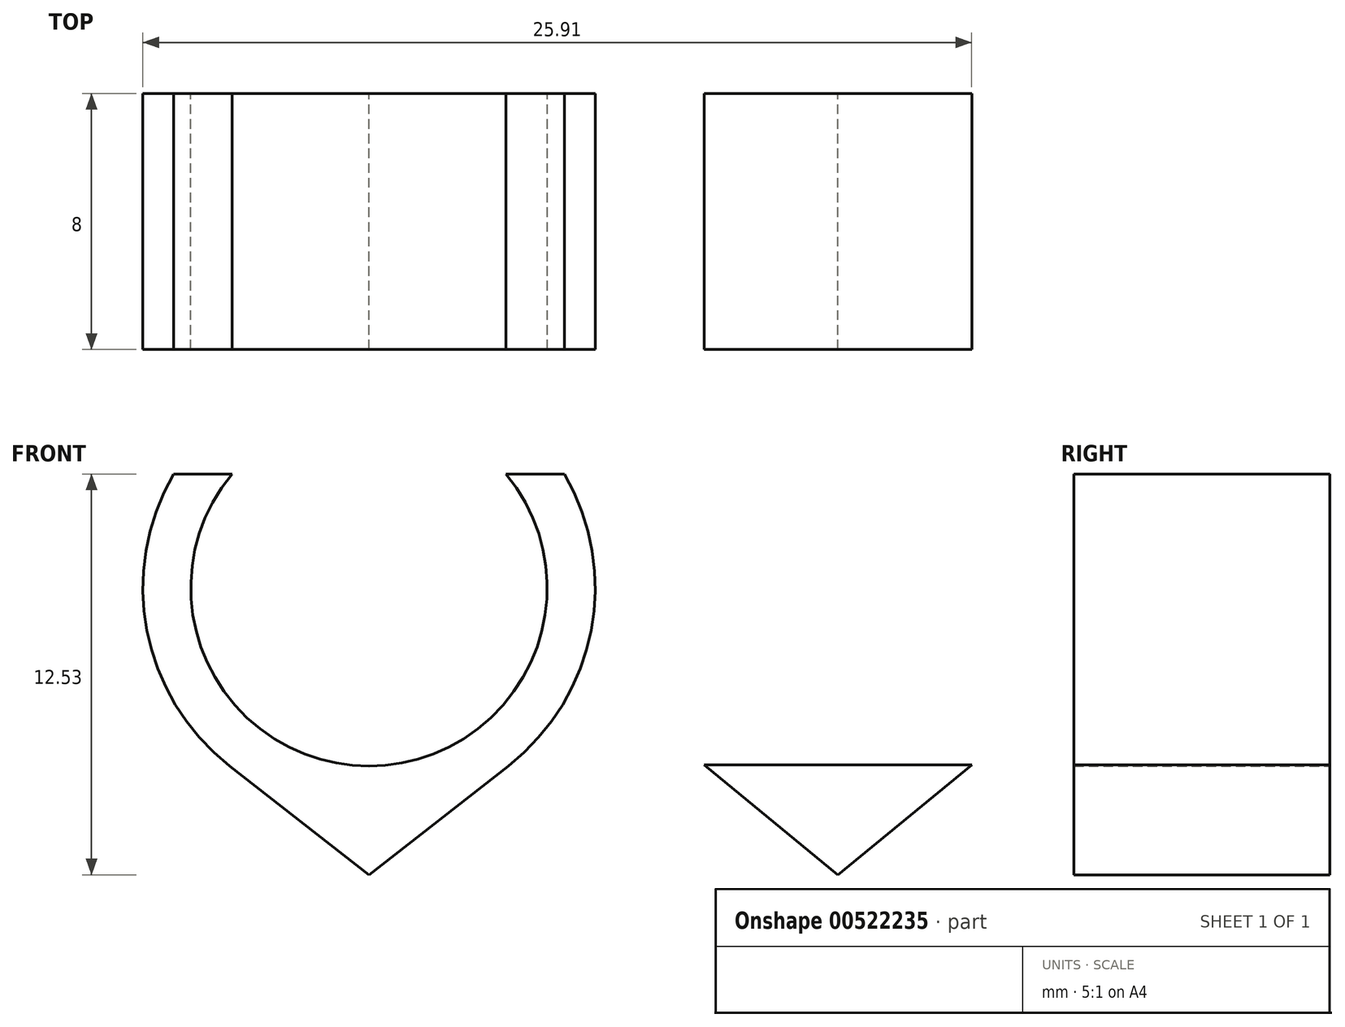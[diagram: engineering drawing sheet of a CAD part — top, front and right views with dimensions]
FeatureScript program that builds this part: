
annotation { "Feature Type Name" : "Feature", "Feature Type Description" : "" }
export const myFeature = defineFeature(function(context is Context, id is Id, definition is map)
    precondition{}
    {
        {
            var Q0;
            Q0=qCreatedBy(makeId("Front.planeOp"),FACE);
            var sketch = newSketch(context, id + "F0", { "sketchPlane" : qUnion([Q0])});
            skArc(sketch, "E0", {"start": v(-6.1, 12.53) * mm, "mid": v(0, 1.9) * mm, "end": v(6.1, 12.53) * mm});
            skLineSegment(sketch, "E1", {"start": v(-4.35, 3.4) * mm, "end": v(0, 0) * mm});
            skLineSegment(sketch, "E2", {"start": v(0, 0) * mm, "end": v(4.35, 3.4) * mm});
            skLineSegment(sketch, "E3", {"start": v(6.1, 12.53) * mm, "end": v(-6.1, 12.53) * mm});
            skArc(sketch, "E4.0", {"start": v(-4.29, 12.53) * mm, "mid": v(0, 3.4) * mm, "end": v(4.29, 12.53) * mm});
            skLineSegment(sketch, "E5", {"start": v(-5, 0) * mm, "end": v(5, 0) * mm});
            skArc(sketch, "E6", {"start": v(8.79, 11.53) * mm, "mid": v(14.66, 1.94) * mm, "end": v(20.53, 11.53) * mm});
            skLineSegment(sketch, "E7", {"start": v(10.47, 3.44) * mm, "end": v(14.66, 0) * mm});
            skLineSegment(sketch, "E8", {"start": v(14.66, 0) * mm, "end": v(18.84, 3.44) * mm});
            skLineSegment(sketch, "E9", {"start": v(20.53, 11.53) * mm, "end": v(8.79, 11.53) * mm});
            skArc(sketch, "E10.0", {"start": v(10.54, 11.53) * mm, "mid": v(14.66, 3.44) * mm, "end": v(18.78, 11.53) * mm});
            skLineSegment(sketch, "E11", {"start": v(9.66, 0) * mm, "end": v(19.66, 0) * mm});
            skLineSegment(sketch, "E12", {"start": v(14.66, 8.53) * mm, "end": v(14.66, 0) * mm});
            skLineSegment(sketch, "E13", {"start": v(-4.35, 3.4) * mm, "end": v(4.35, 3.4) * mm});
            skLineSegment(sketch, "E14", {"start": v(0, 8.97) * mm, "end": v(0, 0) * mm});
            skLineSegment(sketch, "E15", {"start": v(10.47, 3.44) * mm, "end": v(18.84, 3.44) * mm});
            skSolve(sketch);
        }
        {
            var Q0;
            Q0=sQuery(id+"F0.wireOp",EDGE,"E5");
            var Q1;
            {var subQ0=sQuery(id+"F0.wireOp",EDGE,"E1");Q1=makeQuery(id+"F0.imprint","IMPRINT",FACE,{"disambiguationData":[TD([[makeQuery(id+"F0.imprint","IMPRINT",EDGE,{"derivedFrom":subQ0}),1.0]])]});}
            cPlane(context, id + "F1", {"entities" : qUnion([Q0, Q1]), "cplaneType" : CPlaneType.LINE_ANGLE, "offset" : 25 * mm, "angle" : 90 * degree, "width" : 150 * mm, "height" : 150 * mm});
        }
        {
            var Q0;
            Q0=qCreatedBy(id+"F1.planeOp",FACE);
            var sketch = newSketch(context, id + "F2", { "sketchPlane" : qUnion([Q0])});
            skLineSegment(sketch, "E16", {"start": v(0, 0) * mm, "end": v(0, 8) * mm});
            skLineSegment(sketch, "E17.0", {"start": v(9.66, 0) * mm, "end": v(19.66, 0) * mm});
            skLineSegment(sketch, "E18", {"start": v(14.66, 0) * mm, "end": v(14.66, 8) * mm});
            skSolve(sketch);
        }
        {
            var Q0;
            {var subQ0=sQuery(id+"F0.wireOp",EDGE,"E3");var subQ1=sQuery(id+"F0.wireOp",EDGE,"E0");var subQ2=makeQuery(id+"F0.imprint","INTERSECT",VERTEX,{"disambiguationData":[OD(0.0)],"derivedFrom":[subQ1,subQ0]});Q0=makeQuery(id+"F0.imprint","IMPRINT",FACE,{"disambiguationData":[TD([[makeQuery(id+"F0.imprint","IMPRINT",EDGE,{"disambiguationData":[TD([[subQ2,1.0]])],"derivedFrom":subQ0}),1.0]])]});}
            var Q1;
            {var subQ1=sQuery(id+"F0.wireOp",EDGE,"E0");var subQ3=sQuery(id+"F0.wireOp",EDGE,"E14");var subQ4=makeQuery(id+"F0.imprint","INTERSECT",VERTEX,{"derivedFrom":[subQ1,subQ3]});Q1=makeQuery(id+"F0.imprint","IMPRINT",FACE,{"disambiguationData":[TD([[makeQuery(id+"F0.imprint","IMPRINT",EDGE,{"disambiguationData":[TD([[subQ4,1.0]])],"derivedFrom":subQ1}),1.0]])]});}
            var Q2;
            {var subQ0=sQuery(id+"F0.wireOp",EDGE,"E1");Q2=makeQuery(id+"F0.imprint","IMPRINT",FACE,{"disambiguationData":[TD([[makeQuery(id+"F0.imprint","IMPRINT",EDGE,{"derivedFrom":subQ0}),1.0]])]});}
            var Q3;
            {var subQ0=sQuery(id+"F0.wireOp",EDGE,"E2");Q3=makeQuery(id+"F0.imprint","IMPRINT",FACE,{"disambiguationData":[TD([[makeQuery(id+"F0.imprint","IMPRINT",EDGE,{"derivedFrom":subQ0}),1.0]])]});}
            var Q4;
            {var subQ1=sQuery(id+"F0.wireOp",EDGE,"E0");var subQ3=sQuery(id+"F0.wireOp",EDGE,"E14");var subQ4=makeQuery(id+"F0.imprint","INTERSECT",VERTEX,{"derivedFrom":[subQ1,subQ3]});Q4=makeQuery(id+"F0.imprint","IMPRINT",FACE,{"disambiguationData":[TD([[makeQuery(id+"F0.imprint","IMPRINT",EDGE,{"disambiguationData":[TD([[subQ4,-1.0]])],"derivedFrom":subQ1}),1.0]])]});}
            var Q5;
            {var subQ0=sQuery(id+"F0.wireOp",EDGE,"E3");var subQ1=sQuery(id+"F0.wireOp",EDGE,"E0");var subQ2=makeQuery(id+"F0.imprint","INTERSECT",VERTEX,{"disambiguationData":[OD(1.0)],"derivedFrom":[subQ1,subQ0]});Q5=makeQuery(id+"F0.imprint","IMPRINT",FACE,{"disambiguationData":[TD([[makeQuery(id+"F0.imprint","IMPRINT",EDGE,{"disambiguationData":[TD([[subQ2,-1.0]])],"derivedFrom":subQ0}),1.0]])]});}
            var Q6;
            Q6=sQuery(id+"F2.wireOp",EDGE,"E16");
            sweep(context, id + "F3", {"profiles" : qUnion([Q0, Q1, Q2, Q3, Q4, Q5]), "path" : qUnion([Q6])});
        }
        {
            var Q0;
            {var subQ0=sQuery(id+"F0.wireOp",EDGE,"E9");var subQ1=sQuery(id+"F0.wireOp",EDGE,"E6");var subQ2=makeQuery(id+"F0.imprint","INTERSECT",VERTEX,{"disambiguationData":[OD(0.0)],"derivedFrom":[subQ1,subQ0]});Q0=makeQuery(id+"F0.imprint","IMPRINT",FACE,{"disambiguationData":[TD([[makeQuery(id+"F0.imprint","IMPRINT",EDGE,{"disambiguationData":[TD([[subQ2,1.0]])],"derivedFrom":subQ0}),1.0]])]});}
            var Q1;
            {var subQ1=sQuery(id+"F0.wireOp",EDGE,"E6");var subQ3=sQuery(id+"F0.wireOp",EDGE,"E12");var subQ4=makeQuery(id+"F0.imprint","INTERSECT",VERTEX,{"derivedFrom":[subQ1,subQ3]});Q1=makeQuery(id+"F0.imprint","IMPRINT",FACE,{"disambiguationData":[TD([[makeQuery(id+"F0.imprint","IMPRINT",EDGE,{"disambiguationData":[TD([[subQ4,1.0]])],"derivedFrom":subQ1}),1.0]])]});}
            var Q2;
            {var subQ0=sQuery(id+"F0.wireOp",EDGE,"E7");Q2=makeQuery(id+"F0.imprint","IMPRINT",FACE,{"disambiguationData":[TD([[makeQuery(id+"F0.imprint","IMPRINT",EDGE,{"derivedFrom":subQ0}),1.0]])]});}
            var Q3;
            {var subQ0=sQuery(id+"F0.wireOp",EDGE,"E8");Q3=makeQuery(id+"F0.imprint","IMPRINT",FACE,{"disambiguationData":[TD([[makeQuery(id+"F0.imprint","IMPRINT",EDGE,{"derivedFrom":subQ0}),1.0]])]});}
            var Q4;
            {var subQ1=sQuery(id+"F0.wireOp",EDGE,"E6");var subQ3=sQuery(id+"F0.wireOp",EDGE,"E12");var subQ4=makeQuery(id+"F0.imprint","INTERSECT",VERTEX,{"derivedFrom":[subQ1,subQ3]});Q4=makeQuery(id+"F0.imprint","IMPRINT",FACE,{"disambiguationData":[TD([[makeQuery(id+"F0.imprint","IMPRINT",EDGE,{"disambiguationData":[TD([[subQ4,-1.0]])],"derivedFrom":subQ1}),1.0]])]});}
            var Q5;
            {var subQ0=sQuery(id+"F0.wireOp",EDGE,"E9");var subQ1=sQuery(id+"F0.wireOp",EDGE,"E6");var subQ2=makeQuery(id+"F0.imprint","INTERSECT",VERTEX,{"disambiguationData":[OD(1.0)],"derivedFrom":[subQ1,subQ0]});Q5=makeQuery(id+"F0.imprint","IMPRINT",FACE,{"disambiguationData":[TD([[makeQuery(id+"F0.imprint","IMPRINT",EDGE,{"disambiguationData":[TD([[subQ2,-1.0]])],"derivedFrom":subQ0}),1.0]])]});}
            var Q6;
            Q6=sQuery(id+"F2.wireOp",EDGE,"E18");
            sweep(context, id + "F4", {"profiles" : qUnion([Q0, Q1, Q2, Q3, Q4, Q5]), "path" : qUnion([Q6])});
        }
    });
